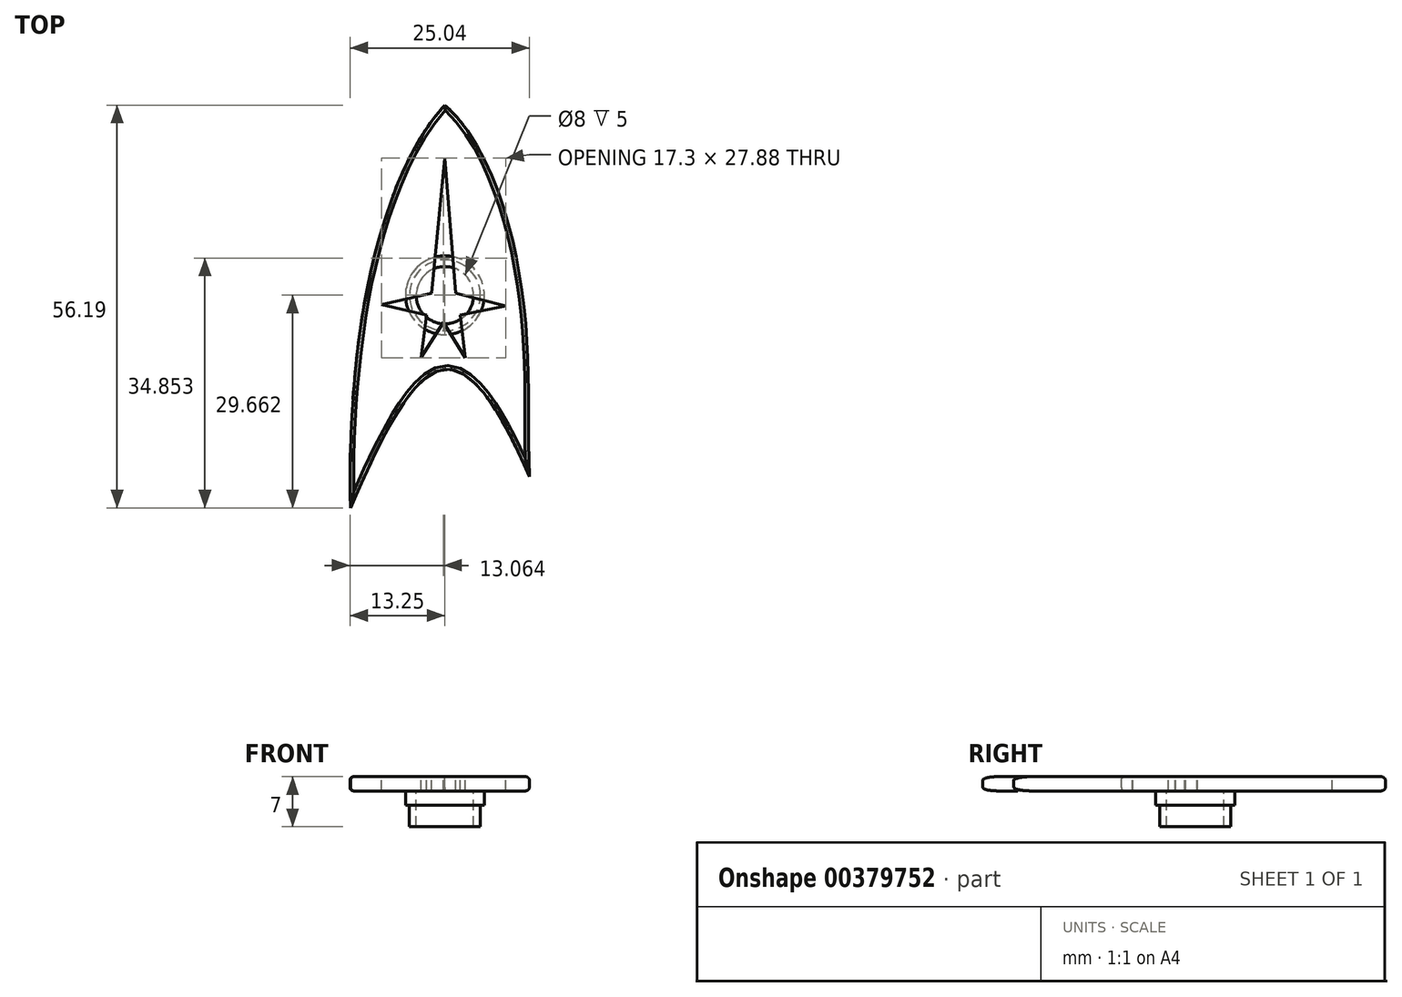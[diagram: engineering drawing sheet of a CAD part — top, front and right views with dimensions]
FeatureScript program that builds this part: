
annotation { "Feature Type Name" : "Feature", "Feature Type Description" : "" }
export const myFeature = defineFeature(function(context is Context, id is Id, definition is map)
    precondition{}
    {
        {
            var Q0;
            Q0=qCreatedBy(makeId("Top.planeOp"),FACE);
            var sketch = newSketch(context, id + "F0", { "sketchPlane" : qUnion([Q0])});
            skLineSegment(sketch, "E0", {"start": v(0, 29.46) * mm, "end": v(-1.83, 10.6) * mm});
            skLineSegment(sketch, "E1", {"start": v(-1.83, 10.6) * mm, "end": v(-8.84, 9) * mm});
            skLineSegment(sketch, "E2", {"start": v(-8.84, 9) * mm, "end": v(-2.56, 7.57) * mm});
            skLineSegment(sketch, "E3", {"start": v(-2.56, 7.57) * mm, "end": v(-3.34, 1.63) * mm});
            skLineSegment(sketch, "E4", {"start": v(-3.34, 1.63) * mm, "end": v(-0.2, 6.56) * mm});
            skLineSegment(sketch, "E5.MirrorCS", {"start": v(0, 29.46) * mm, "end": v(1.5, 10.58) * mm});
            skLineSegment(sketch, "E6.MirrorCS", {"start": v(1.5, 10.58) * mm, "end": v(8.47, 8.84) * mm});
            skLineSegment(sketch, "E7.MirrorCS", {"start": v(8.47, 8.84) * mm, "end": v(2.16, 7.53) * mm});
            skLineSegment(sketch, "E8.MirrorCS", {"start": v(2.16, 7.53) * mm, "end": v(2.83, 1.57) * mm});
            skLineSegment(sketch, "E9.MirrorCS", {"start": v(2.83, 1.57) * mm, "end": v(-0.2, 6.56) * mm});
            skLineSegment(sketch, "E10", {"start": v(-0.2, 1.55) * mm, "end": v(0, 34.2) * mm, "construction": true});
            skSolve(sketch);
        }
        {
            var Q0;
            Q0=qCreatedBy(makeId("Top.planeOp"),FACE);
            var sketch = newSketch(context, id + "F1", { "sketchPlane" : qUnion([Q0])});
            skFitSpline(sketch, "E11", {"points": [v(0, 36.85) * mm, v(-10.87, 11.1) * mm, v(-13.16, -19.34) * mm], "startDerivative": vector(-30.04, -32.08) * mm, "endDerivative": vector(1.6, -35.75) * mm});
            skFitSpline(sketch, "E12", {"points": [v(0, 36.85) * mm, v(10.87, 9.96) * mm, v(11.79, -15) * mm], "startDerivative": vector(35.32, -31.44) * mm, "endDerivative": vector(1.99, -41.42) * mm});
            skFitSpline(sketch, "E13", {"points": [v(-13.16, -19.34) * mm, v(0, 0) * mm, v(11.79, -15) * mm], "startDerivative": vector(27.44, 64.04) * mm, "endDerivative": vector(26.05, -60.8) * mm});
            skLineSegment(sketch, "E14.0", {"start": v(-0.9, 9.8) * mm, "end": v(-4.35, 9) * mm});
            skLineSegment(sketch, "E14.1", {"start": v(-4.35, 9) * mm, "end": v(-1.45, 8.34) * mm});
            skLineSegment(sketch, "E14.2", {"start": v(-1.45, 8.34) * mm, "end": v(-1.76, 5.98) * mm});
            skLineSegment(sketch, "E14.3", {"start": v(-1.76, 5.98) * mm, "end": v(-0.2, 8.46) * mm});
            skLineSegment(sketch, "E14.4", {"start": v(1.33, 5.95) * mm, "end": v(-0.2, 8.46) * mm});
            skLineSegment(sketch, "E14.5", {"start": v(1.07, 8.32) * mm, "end": v(1.33, 5.95) * mm});
            skLineSegment(sketch, "E14.6", {"start": v(3.98, 8.93) * mm, "end": v(1.07, 8.32) * mm});
            skLineSegment(sketch, "E14.7", {"start": v(0.55, 9.78) * mm, "end": v(3.98, 8.93) * mm});
            skLineSegment(sketch, "E14.8", {"start": v(-0.1, 18.06) * mm, "end": v(0.55, 9.78) * mm});
            skLineSegment(sketch, "E14.9", {"start": v(-0.1, 18.06) * mm, "end": v(-0.9, 9.8) * mm});
            skSolve(sketch);
        }
        {
            var Q0;
            Q0=makeQuery(id+"F1.imprint","IMPRINT",FACE,{"disambiguationData":[TD([[makeQuery(id+"F1.imprint","IMPRINT",EDGE,{"derivedFrom":sQuery(id+"F1.wireOp",EDGE,"E11")}),1.0]])]});
            extrude(context, id + "F2", {"entities" : qUnion([Q0]), "flatOperationType" : FlatOperationType.REMOVE, "oppositeDirection" : true, "depth" : 2 * mm, "offsetDistance" : 25 * mm, "domain" : OperationDomain.MODEL});
        }
        {
            var Q0;
            Q0=makeQuery(id+"F0.imprint","IMPRINT",FACE,{"disambiguationData":[TD([[makeQuery(id+"F0.imprint","IMPRINT",EDGE,{"derivedFrom":sQuery(id+"F0.wireOp",EDGE,"E0")}),1.0]])]});
            extrude(context, id + "F3", {"entities" : qUnion([Q0]), "operationType" : NewBodyOperationType.REMOVE, "oppositeDirection" : true, "depth" : 3 * mm, "offsetDistance" : 25 * mm});
        }
        {
            var Q0;
            Q0=makeQuery(id+"F2.opExtrude","CAP_EDGE",EDGE,{"disambiguationData":[OSD([sQuery(id+"F1.wireOp",EDGE,"E12")])],"isStart":true});
            var Q1;
            Q1=makeQuery(id+"F2.opExtrude","CAP_EDGE",EDGE,{"disambiguationData":[OSD([sQuery(id+"F1.wireOp",EDGE,"E11")])],"isStart":true});
            var Q2;
            Q2=makeQuery(id+"F2.opExtrude","CAP_EDGE",EDGE,{"disambiguationData":[OSD([sQuery(id+"F1.wireOp",EDGE,"E13")])],"isStart":true});
            var Q3;
            Q3=makeQuery(id+"F2.opExtrude","CAP_EDGE",EDGE,{"disambiguationData":[OSD([sQuery(id+"F1.wireOp",EDGE,"E12")])],"isStart":false});
            var Q4;
            Q4=makeQuery(id+"F2.opExtrude","CAP_EDGE",EDGE,{"disambiguationData":[OSD([sQuery(id+"F1.wireOp",EDGE,"E11")])],"isStart":false});
            var Q5;
            Q5=makeQuery(id+"F2.opExtrude","CAP_EDGE",EDGE,{"disambiguationData":[OSD([sQuery(id+"F1.wireOp",EDGE,"E13")])],"isStart":false});
            fillet(context, id + "F4", {"entities" : qUnion([Q0, Q1, Q2, Q3, Q4, Q5]), "radius" : .5 * mm, "tangentPropagation" : true, "allowEdgeOverflow" : false});
        }
        {
            var Q0;
            Q0=makeQuery(id+"F2.opExtrude","CAP_FACE",FACE,{"disambiguationData":[OSD([sQuery(id+"F1.wireOp",EDGE,"E11"),sQuery(id+"F1.wireOp",EDGE,"E12"),sQuery(id+"F1.wireOp",EDGE,"E13")])],"isStart":false});
            var sketch = newSketch(context, id + "F5", { "sketchPlane" : qUnion([Q0])});
            skCircle(sketch, "E15", {"center": v(0, -10.32) * mm, "radius": 4 * mm});
            skCircle(sketch, "E16", {"center": v(0, -10.32) * mm, "radius": 4.95 * mm});
            skCircle(sketch, "E17", {"center": v(0, -10.32) * mm, "radius": 5.5 * mm});
            skSolve(sketch);
        }
        {
            var Q0;
            Q0=makeQuery(id+"F5.imprint","IMPRINT",FACE,{"disambiguationData":[TD([[makeQuery(id+"F5.imprint","IMPRINT",EDGE,{"derivedFrom":sQuery(id+"F5.wireOp",EDGE,"E15")}),-1.0]])]});
            extrude(context, id + "F6", {"entities" : qUnion([Q0]), "operationType" : NewBodyOperationType.ADD, "depth" : 5 * mm, "offsetDistance" : 25 * mm});
        }
        {
            var Q0;
            Q0=makeQuery(id+"F5.imprint","IMPRINT",FACE,{"disambiguationData":[TD([[makeQuery(id+"F5.imprint","IMPRINT",EDGE,{"derivedFrom":sQuery(id+"F5.wireOp",EDGE,"E16")}),-1.0]])]});
            extrude(context, id + "F7", {"entities" : qUnion([Q0]), "operationType" : NewBodyOperationType.ADD, "depth" : 2 * mm, "offsetDistance" : 25 * mm});
        }
    });
